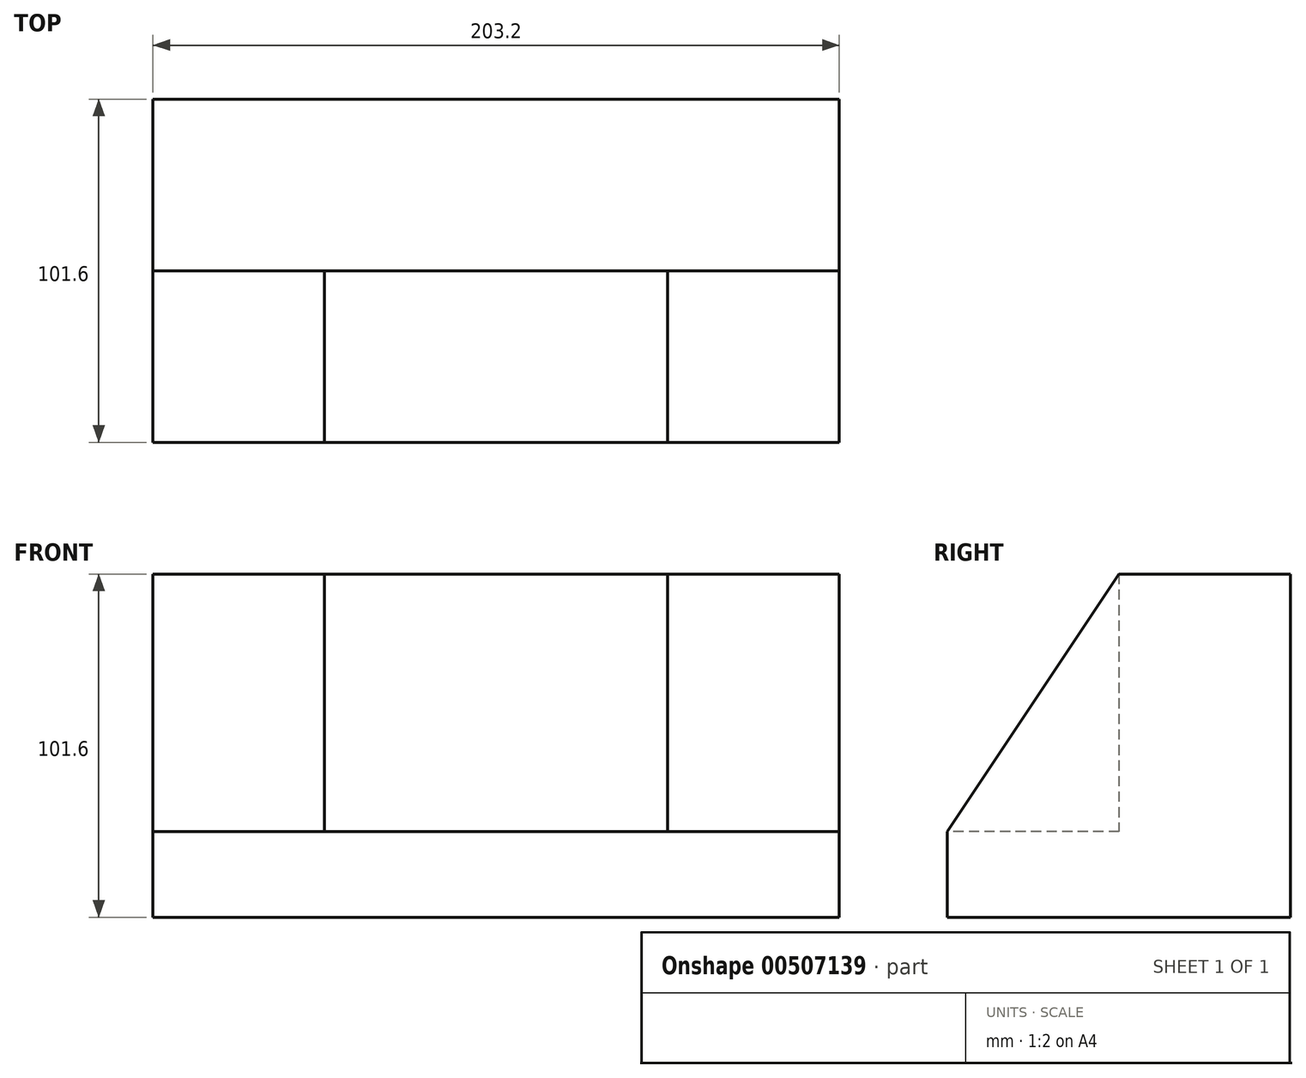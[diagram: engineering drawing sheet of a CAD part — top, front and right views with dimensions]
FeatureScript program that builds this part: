
annotation { "Feature Type Name" : "Feature", "Feature Type Description" : "" }
export const myFeature = defineFeature(function(context is Context, id is Id, definition is map)
    precondition{}
    {
        {
            var Q0;
            Q0=qCreatedBy(makeId("Front.planeOp"),FACE);
            var sketch = newSketch(context, id + "F0", { "sketchPlane" : qUnion([Q0])});
            skLineSegment(sketch, "E0.bottom", {"start": v(103.88, -50.8) * mm, "end": v(-99.32, -50.8) * mm});
            skLineSegment(sketch, "E0.top", {"start": v(103.88, 50.8) * mm, "end": v(-99.32, 50.8) * mm});
            skLineSegment(sketch, "E0.left", {"start": v(103.88, -50.8) * mm, "end": v(103.88, 50.8) * mm});
            skLineSegment(sketch, "E0.right", {"start": v(-99.32, -50.8) * mm, "end": v(-99.32, 50.8) * mm});
            skPoint(sketch, "E0.middle", {"position": v(2.28, 0) * mm});
            skSolve(sketch);
        }
        {
            var Q0;
            Q0 = qSketchRegion(id + "F0", true);
            extrude(context, id + "F1", {"entities" : qUnion([Q0]), "depth" : 101.6 * mm});
        }
        {
            var Q0;
            Q0=makeQuery(id+"F1.opExtrude","SWEPT_FACE",FACE,{"disambiguationData":[OSD([sQuery(id+"F0.wireOp",EDGE,"E0.right")])]});
            var sketch = newSketch(context, id + "F2", { "sketchPlane" : qUnion([Q0])});
            skLineSegment(sketch, "E1", {"start": v(50.8, 50.8) * mm, "end": v(50.8, -25.4) * mm});
            skLineSegment(sketch, "E2", {"start": v(50.8, -25.4) * mm, "end": v(101.6, -25.4) * mm});
            skSolve(sketch);
        }
        {
            var Q0;
            {var subQ0=sQuery(id+"F2.wireOp",EDGE,"E1");Q0=makeQuery(id+"F2.imprint","IMPRINT",FACE,{"disambiguationData":[TD([[makeQuery(id+"F2.imprint","IMPRINT",EDGE,{"derivedFrom":subQ0}),1.0]])]});}
            extrude(context, id + "F3", {"entities" : qUnion([Q0]), "operationType" : NewBodyOperationType.REMOVE, "oppositeDirection" : true, "depth" : 203.2 * mm});
        }
        {
            var Q0;
            Q0=makeQuery(id+"F1.opExtrude","SWEPT_FACE",FACE,{"disambiguationData":[OSD([sQuery(id+"F0.wireOp",EDGE,"E0.right")])]});
            var sketch = newSketch(context, id + "F4", { "sketchPlane" : qUnion([Q0])});
            skLineSegment(sketch, "E3", {"start": v(50.8, 50.8) * mm, "end": v(101.6, -25.4) * mm});
            skLineSegment(sketch, "E4", {"start": v(101.6, -25.4) * mm, "end": v(50.8, -25.4) * mm});
            skLineSegment(sketch, "E5", {"start": v(50.8, -25.4) * mm, "end": v(50.8, 50.8) * mm});
            skSolve(sketch);
        }
        {
            var Q0;
            Q0=makeQuery(id+"F4.imprint","IMPRINT",FACE,{"disambiguationData":[TD([[makeQuery(id+"F4.imprint","IMPRINT",EDGE,{"derivedFrom":sQuery(id+"F4.wireOp",EDGE,"E3")}),-1.0]])]});
            extrude(context, id + "F5", {"entities" : qUnion([Q0]), "operationType" : NewBodyOperationType.ADD, "oppositeDirection" : true, "depth" : 50.8 * mm});
        }
        {
            var Q0;
            Q0=makeQuery(id+"F1.opExtrude","SWEPT_FACE",FACE,{"disambiguationData":[OSD([sQuery(id+"F0.wireOp",EDGE,"E0.left")])]});
            var sketch = newSketch(context, id + "F6", { "sketchPlane" : qUnion([Q0])});
            skLineSegment(sketch, "E6", {"start": v(-50.8, 50.8) * mm, "end": v(-50.8, -25.4) * mm});
            skLineSegment(sketch, "E7", {"start": v(-50.8, -25.4) * mm, "end": v(-101.6, -25.4) * mm});
            skLineSegment(sketch, "E8", {"start": v(-101.6, -25.4) * mm, "end": v(-50.8, 50.8) * mm});
            skSolve(sketch);
        }
        {
            var Q0;
            Q0 = qSketchRegion(id + "F6", true);
            extrude(context, id + "F7", {"entities" : qUnion([Q0]), "operationType" : NewBodyOperationType.ADD, "oppositeDirection" : true, "depth" : 50.8 * mm});
        }
    });
